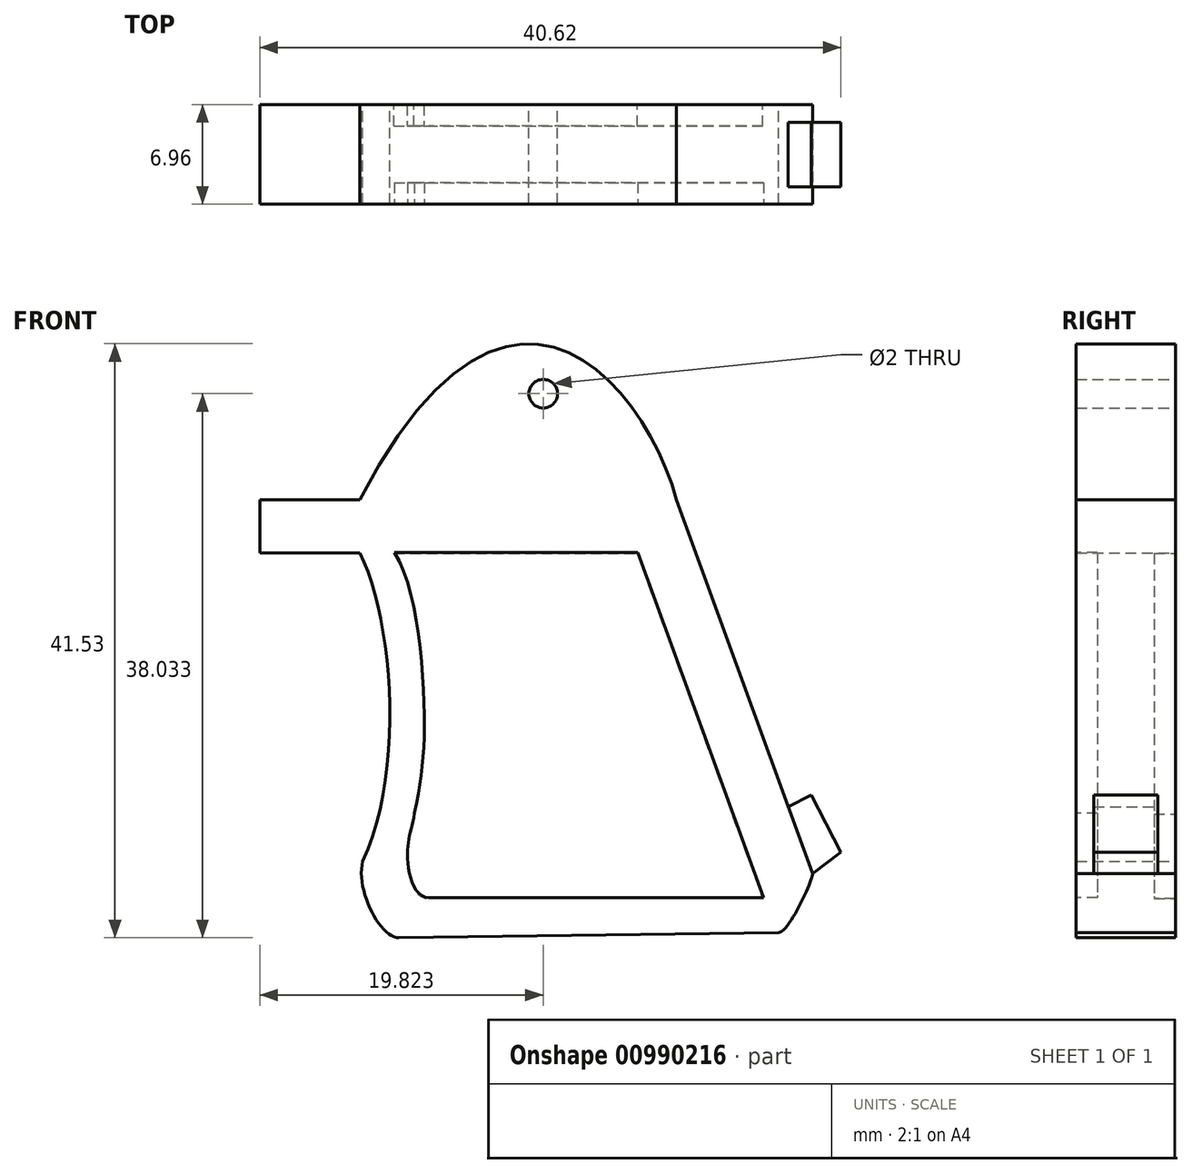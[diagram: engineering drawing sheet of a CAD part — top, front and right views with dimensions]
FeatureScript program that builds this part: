
annotation { "Feature Type Name" : "Feature", "Feature Type Description" : "" }
export const myFeature = defineFeature(function(context is Context, id is Id, definition is map)
    precondition{}
    {
        {
            var Q0;
            Q0=qCreatedBy(makeId("Front.planeOp"),FACE);
            var sketch = newSketch(context, id + "F0", { "sketchPlane" : qUnion([Q0])});
            skLineSegment(sketch, "E0", {"start": v(0, 21.44) * mm, "end": v(62.3, 21.44) * mm, "construction": true});
            skLineSegment(sketch, "E1", {"start": v(34.3, -27.32) * mm, "end": v(36.18, -31.96) * mm, "construction": true});
            skArc(sketch, "E2", {"start": v(36.18, -31.96) * mm, "mid": v(59.6, -10.33) * mm, "end": v(62.3, 21.44) * mm, "construction": true});
            skCircle(sketch, "E3", {"center": v(3.5, 17.52) * mm, "radius": 1 * mm, "construction": true});
            skCircle(sketch, "E4", {"center": v(3.5, 6.66) * mm, "radius": 1 * mm, "construction": true});
            skCircle(sketch, "E5", {"center": v(54.67, 14.2) * mm, "radius": 1 * mm, "construction": true});
            skCircle(sketch, "E6", {"center": v(37.59, -28.7) * mm, "radius": 1 * mm, "construction": true});
            skCircle(sketch, "E7", {"center": v(19.82, 11.13) * mm, "radius": 1 * mm});
            skLineSegment(sketch, "E8", {"start": v(0, 21.44) * mm, "end": v(0, 3.73) * mm, "construction": true});
            skLineSegment(sketch, "E9", {"start": v(6.67, 3.73) * mm, "end": v(6.67, 12.79) * mm, "construction": true});
            skFitSpline(sketch, "E10", {"points": [v(34.3, -27.32) * mm, v(52.88, -13.89) * mm, v(58.33, 2.5) * mm], "startDerivative": vector(28.58, 7.3) * mm, "endDerivative": vector(-4.8, 17.89) * mm, "construction": true});
            skLineSegment(sketch, "E11", {"start": v(58.33, 2.5) * mm, "end": v(53.49, 5.5) * mm, "construction": true});
            skFitSpline(sketch, "E12", {"points": [v(6.67, 12.79) * mm, v(52.3, 6.17) * mm], "startDerivative": vector(41.09, 30.77) * mm, "endDerivative": vector(41.7, -23.1) * mm, "construction": true});
            skLineSegment(sketch, "E13", {"start": v(52.1, -0.76) * mm, "end": v(57.8, -1.52) * mm, "construction": true});
            skLineSegment(sketch, "E14", {"start": v(57.8, -1.52) * mm, "end": v(58.33, 2.5) * mm, "construction": true});
            skLineSegment(sketch, "E15", {"start": v(52.1, -0.76) * mm, "end": v(53.49, 5.5) * mm, "construction": true});
            skLineSegment(sketch, "E16", {"start": v(54.95, -1.14) * mm, "end": v(55.9, 4) * mm, "construction": true});
            skLineSegment(sketch, "E17", {"start": v(0, 0) * mm, "end": v(0, 3.73) * mm});
            skLineSegment(sketch, "E18", {"start": v(0, 3.73) * mm, "end": v(7, 3.73) * mm});
            skLineSegment(sketch, "E19", {"start": v(0, 0) * mm, "end": v(7, 0) * mm});
            skFitSpline(sketch, "E20", {"points": [v(7, 0) * mm, v(7.2, -21.56) * mm], "startDerivative": vector(6.85, -13.57) * mm, "endDerivative": vector(-8.94, -19.15) * mm});
            skLineSegment(sketch, "E21", {"start": v(36.33, -26.67) * mm, "end": v(36.26, -26.54) * mm, "construction": true});
            skLineSegment(sketch, "E22", {"start": v(36.26, -26.54) * mm, "end": v(9.74, -26.9) * mm});
            skFitSpline(sketch, "E23", {"points": [v(7.2, -21.56) * mm, v(9.74, -26.9) * mm], "startDerivative": vector(-1.53, -5.77) * mm, "endDerivative": vector(4.06, 0.09) * mm});
            skFitSpline(sketch, "E24", {"points": [v(7, 3.73) * mm, v(29.13, 3.73) * mm], "startDerivative": vector(31, 59.2) * mm, "endDerivative": vector(6.79, -24.68) * mm});
            skLineSegment(sketch, "E25", {"start": v(29.13, 3.73) * mm, "end": v(38.66, -22.42) * mm});
            skFitSpline(sketch, "E26", {"points": [v(38.66, -22.42) * mm, v(36.26, -26.54) * mm], "startDerivative": vector(0.1, -0.88) * mm, "endDerivative": vector(-2.4, -0.14) * mm});
            skLineSegment(sketch, "E27", {"start": v(38.66, -22.42) * mm, "end": v(40.62, -20.92) * mm});
            skLineSegment(sketch, "E28", {"start": v(40.62, -20.92) * mm, "end": v(38.56, -16.92) * mm});
            skLineSegment(sketch, "E29", {"start": v(38.56, -16.92) * mm, "end": v(36.96, -17.74) * mm});
            skLineSegment(sketch, "E30", {"start": v(39.59, -18.92) * mm, "end": v(37.73, -19.87) * mm});
            skLineSegment(sketch, "E31", {"start": v(33.62, -26.57) * mm, "end": v(33.62, -24.12) * mm, "construction": true});
            skLineSegment(sketch, "E32", {"start": v(7, 0) * mm, "end": v(9.45, 0) * mm, "construction": true});
            skFitSpline(sketch, "E33", {"points": [v(9.45, 0) * mm, v(11.54, -11.3) * mm, v(10.85, -18.22) * mm], "startDerivative": vector(8.24, -12.6) * mm, "endDerivative": vector(-3.43, -16.2) * mm});
            skLineSegment(sketch, "E34", {"start": v(32.2, -24.12) * mm, "end": v(11.88, -24.12) * mm});
            skFitSpline(sketch, "E35", {"points": [v(10.85, -18.22) * mm, v(10.36, -21.12) * mm, v(11.88, -24.12) * mm], "startDerivative": vector(-1.11, -7.4) * mm, "endDerivative": vector(6.61, 0.06) * mm});
            skLineSegment(sketch, "E36", {"start": v(9.45, 0) * mm, "end": v(26.46, 0) * mm});
            skLineSegment(sketch, "E37", {"start": v(26.46, 0) * mm, "end": v(35.25, -24.12) * mm});
            skLineSegment(sketch, "E38", {"start": v(35.25, -24.12) * mm, "end": v(32.2, -24.12) * mm});
            skLineSegment(sketch, "E39", {"start": v(17.97, -26.78) * mm, "end": v(17.97, -26.79) * mm, "construction": true});
            skLineSegment(sketch, "E40", {"start": v(52.3, 6.17) * mm, "end": v(53.49, 5.5) * mm, "construction": true});
            skSolve(sketch);
        }
        {
            var Q0;
            Q0=makeQuery(id+"F0.imprint","IMPRINT",FACE,{"disambiguationData":[TD([[makeQuery(id+"F0.imprint","IMPRINT",EDGE,{"derivedFrom":sQuery(id+"F0.wireOp",EDGE,"E7")}),-1.0]])]});
            var Q1;
            Q1=makeQuery(id+"F0.imprint","IMPRINT",FACE,{"disambiguationData":[TD([[makeQuery(id+"F0.imprint","IMPRINT",EDGE,{"derivedFrom":sQuery(id+"F0.wireOp",EDGE,"E33")}),1.0]])]});
            extrude(context, id + "F1", {"entities" : qUnion([Q0, Q1]), "endBound" : BoundingType.SYMMETRIC, "depth" : 6.95 * mm, "offsetDistance" : 25 * mm});
        }
        {
            var Q0;
            {var subQ0=sQuery(id+"F0.wireOp",EDGE,"E29");Q0=makeQuery(id+"F0.imprint","IMPRINT",FACE,{"disambiguationData":[TD([[makeQuery(id+"F0.imprint","IMPRINT",EDGE,{"derivedFrom":subQ0}),1.0]])]});}
            var Q1;
            {var subQ0=sQuery(id+"F0.wireOp",EDGE,"E27");Q1=makeQuery(id+"F0.imprint","IMPRINT",FACE,{"disambiguationData":[TD([[makeQuery(id+"F0.imprint","IMPRINT",EDGE,{"derivedFrom":subQ0}),1.0]])]});}
            extrude(context, id + "F2", {"entities" : qUnion([Q0, Q1]), "operationType" : NewBodyOperationType.ADD, "endBound" : BoundingType.SYMMETRIC, "depth" : 4.5 * mm, "offsetDistance" : 25 * mm});
        }
        {
            var Q0;
            Q0=makeQuery(id+"F1.opExtrude","CAP_FACE",FACE,{"disambiguationData":[OSD([sQuery(id+"F0.wireOp",EDGE,"E7"),sQuery(id+"F0.wireOp",EDGE,"E17"),sQuery(id+"F0.wireOp",EDGE,"E18"),sQuery(id+"F0.wireOp",EDGE,"E19"),sQuery(id+"F0.wireOp",EDGE,"E20"),sQuery(id+"F0.wireOp",EDGE,"E22"),sQuery(id+"F0.wireOp",EDGE,"E23"),sQuery(id+"F0.wireOp",EDGE,"E24"),sQuery(id+"F0.wireOp",EDGE,"E25"),sQuery(id+"F0.wireOp",EDGE,"E26")])],"isStart":false});
            var sketch = newSketch(context, id + "F3", { "sketchPlane" : qUnion([Q0])});
            skFitSpline(sketch, "E41", {"points": [v(9.4, 0.03) * mm, v(11.5, -11.26) * mm, v(10.82, -18.18) * mm], "startDerivative": vector(8.24, -12.6) * mm, "endDerivative": vector(-3.43, -16.2) * mm});
            skLineSegment(sketch, "E42", {"start": v(32.16, -24.09) * mm, "end": v(11.84, -24.09) * mm});
            skFitSpline(sketch, "E43", {"points": [v(10.82, -18.18) * mm, v(10.32, -21.1) * mm, v(11.84, -24.09) * mm], "startDerivative": vector(-1.11, -7.4) * mm, "endDerivative": vector(6.61, 0.06) * mm});
            skLineSegment(sketch, "E44", {"start": v(9.4, 0.03) * mm, "end": v(26.42, 0.03) * mm});
            skLineSegment(sketch, "E45", {"start": v(26.42, 0.03) * mm, "end": v(35.21, -24.09) * mm});
            skLineSegment(sketch, "E46", {"start": v(35.21, -24.09) * mm, "end": v(32.16, -24.09) * mm});
            skSolve(sketch);
        }
        {
            var Q0;
            Q0 = qSketchRegion(id + "F3", true);
            extrude(context, id + "F4", {"entities" : qUnion([Q0]), "operationType" : NewBodyOperationType.REMOVE, "oppositeDirection" : true, "depth" : 1.5 * mm, "offsetDistance" : 25 * mm});
        }
        {
            var Q0;
            Q0=makeQuery(id+"F1.opExtrude","CAP_FACE",FACE,{"disambiguationData":[OSD([sQuery(id+"F0.wireOp",EDGE,"E7"),sQuery(id+"F0.wireOp",EDGE,"E17"),sQuery(id+"F0.wireOp",EDGE,"E18"),sQuery(id+"F0.wireOp",EDGE,"E19"),sQuery(id+"F0.wireOp",EDGE,"E20"),sQuery(id+"F0.wireOp",EDGE,"E22"),sQuery(id+"F0.wireOp",EDGE,"E23"),sQuery(id+"F0.wireOp",EDGE,"E24"),sQuery(id+"F0.wireOp",EDGE,"E25"),sQuery(id+"F0.wireOp",EDGE,"E26")])],"isStart":true});
            var sketch = newSketch(context, id + "F5", { "sketchPlane" : qUnion([Q0])});
            skLineSegment(sketch, "E47.MirrorCS", {"start": v(-35.17, -24.15) * mm, "end": v(-32.13, -24.15) * mm});
            skFitSpline(sketch, "E48.MirrorCS", {"points": [v(-10.78, -18.24) * mm, v(-10.29, -21.15) * mm, v(-11.8, -24.15) * mm], "startDerivative": vector(1.11, -7.4) * mm, "endDerivative": vector(-6.61, 0.06) * mm});
            skLineSegment(sketch, "E49.MirrorCS", {"start": v(-26.39, -0.03) * mm, "end": v(-35.17, -24.15) * mm});
            skFitSpline(sketch, "E50.MirrorCS", {"points": [v(-9.37, -0.03) * mm, v(-11.47, -11.32) * mm, v(-10.78, -18.24) * mm], "startDerivative": vector(-8.24, -12.6) * mm, "endDerivative": vector(3.43, -16.2) * mm});
            skLineSegment(sketch, "E51.MirrorCS", {"start": v(-32.13, -24.15) * mm, "end": v(-11.8, -24.15) * mm});
            skLineSegment(sketch, "E52.MirrorCS", {"start": v(-9.37, -0.03) * mm, "end": v(-26.39, -0.03) * mm});
            skSolve(sketch);
        }
        {
            var Q0;
            Q0 = qSketchRegion(id + "F5", true);
            extrude(context, id + "F6", {"entities" : qUnion([Q0]), "operationType" : NewBodyOperationType.REMOVE, "oppositeDirection" : true, "depth" : 1.5 * mm, "offsetDistance" : 25 * mm});
        }
    });
